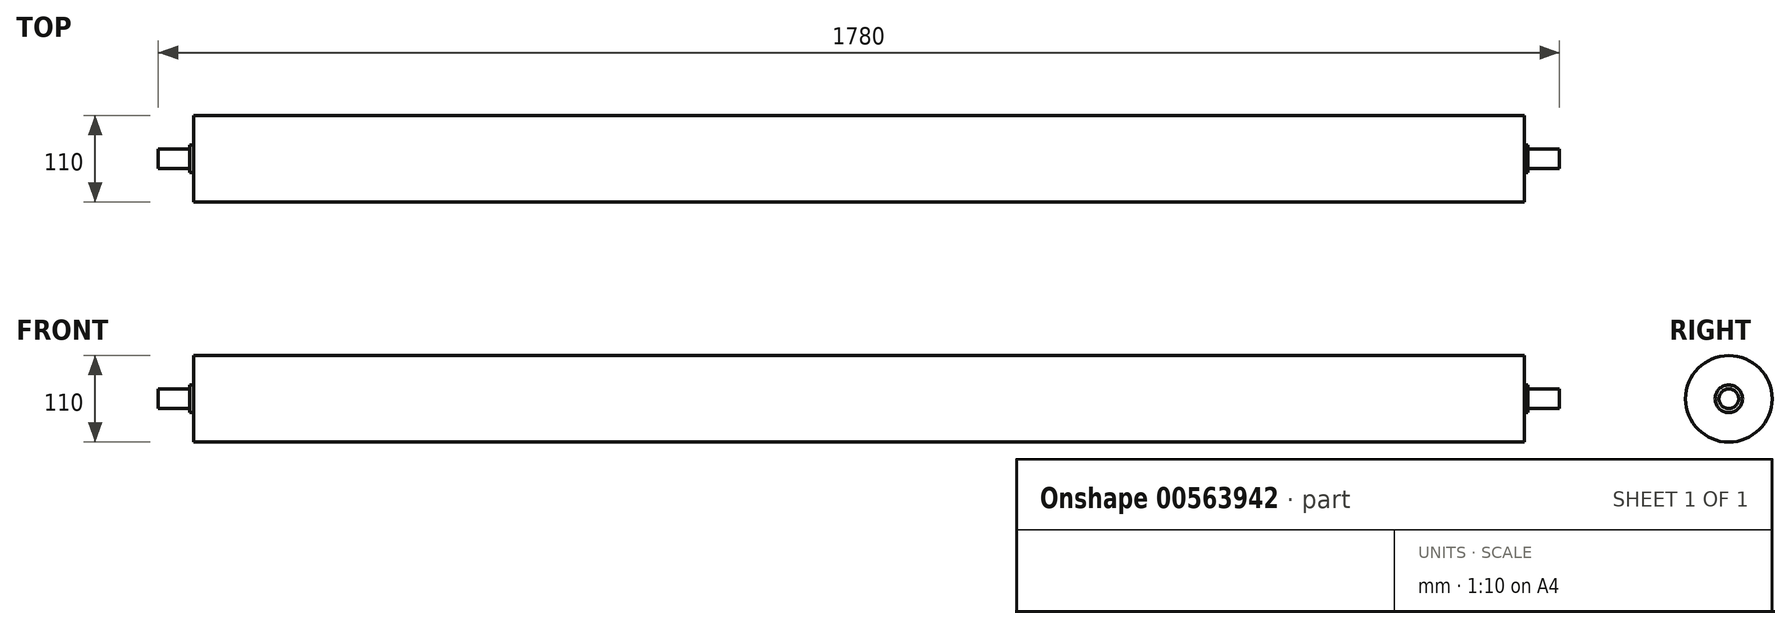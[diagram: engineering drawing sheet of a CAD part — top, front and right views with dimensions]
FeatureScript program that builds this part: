
annotation { "Feature Type Name" : "Feature", "Feature Type Description" : "" }
export const myFeature = defineFeature(function(context is Context, id is Id, definition is map)
    precondition{}
    {
        {
            var Q0;
            Q0=qCreatedBy(makeId("Front.planeOp"),FACE);
            var sketch = newSketch(context, id + "F0", { "sketchPlane" : qUnion([Q0])});
            skLineSegment(sketch, "E0", {"start": v(0, 0) * mm, "end": v(-890, 0) * mm});
            skLineSegment(sketch, "E1", {"start": v(-890, 0) * mm, "end": v(-890, 12.5) * mm});
            skLineSegment(sketch, "E2", {"start": v(-890, 12.5) * mm, "end": v(-850, 12.5) * mm});
            skLineSegment(sketch, "E3", {"start": v(-850, 12.5) * mm, "end": v(-850, 17.5) * mm});
            skLineSegment(sketch, "E4", {"start": v(-850, 17.5) * mm, "end": v(-845, 17.5) * mm});
            skLineSegment(sketch, "E5", {"start": v(-845, 17.5) * mm, "end": v(-845, 55) * mm});
            skLineSegment(sketch, "E6", {"start": v(-845, 55) * mm, "end": v(845, 55) * mm});
            skLineSegment(sketch, "E7", {"start": v(845, 55) * mm, "end": v(845, 17.5) * mm});
            skLineSegment(sketch, "E8", {"start": v(845, 17.5) * mm, "end": v(850, 17.5) * mm});
            skLineSegment(sketch, "E9", {"start": v(850, 17.5) * mm, "end": v(850, 12.5) * mm});
            skLineSegment(sketch, "E10", {"start": v(850, 12.5) * mm, "end": v(890, 12.5) * mm});
            skLineSegment(sketch, "E11", {"start": v(890, 12.5) * mm, "end": v(890, 0) * mm});
            skLineSegment(sketch, "E12", {"start": v(890, 0) * mm, "end": v(0, 0) * mm});
            skLineSegment(sketch, "E13", {"start": v(-776.42, 0) * mm, "end": v(773, 0) * mm, "construction": true});
            skSolve(sketch);
        }
        {
            var Q0;
            Q0=makeQuery(id+"F0.imprint","IMPRINT",FACE,{"disambiguationData":[TD([[makeQuery(id+"F0.imprint","IMPRINT",EDGE,{"derivedFrom":sQuery(id+"F0.wireOp",EDGE,"E0")}),-1.0]])]});
            var Q1;
            Q1=sQuery(id+"F0.wireOp",EDGE,"E13");
            revolve(context, id + "F1", {"entities" : qUnion([Q0]), "axis" : qUnion([Q1]), "revolveType" : RevolveType.FULL});
        }
    });
